# Revit family: IS_Extra_T3740_BIM_NL
name_source: partatom
category: Plumbing Fixtures
units: mm (PartAtom-declared; Revit-internal decimal feet)

## family parameters
Always vertical = No
Cut with Voids When Loaded = No
OmniClass Number = 23.45.05.14.14
OmniClass Title = Sinks/Lavatories
Part Type = Normal
Room Calculation Point = No
Round Connector Dimension = Use Diameter
Shared = No
Work Plane-Based = No

## types (1)
- T374001 - Extra Square Vessel 60x40 N with overflow and without tapholes - White
    Accessories = https://www.idealstandard.nl
    Afmetingen = 600 x 400 x 125 mm
    Afwerking = Weiß
    AreaMeasurement = Internal
    AreaUnits = Millimetres
    Artikelnummer = T374001
    Artikelomschrijving = Zusätzliches Gefäßbecken 60 x 40 cm, keine Hahnlöcher, kein Überlauf, glänzend weiß
    Artikelreferentie = Quadratisches Gefäß 60x40 N mit Überlauf und ohne Stichlöcher - Weiß
    AssetType = Fixed
    Auteur = Ideal Standard
    BIMObjectName = IS_IdealStandard_Wall-hungwashbasins_Extra_T3740
    BIMobject category = Basins
    BIMobject category code = sanitary-basins
    BIMobject main category = Sanitary
    BIMobject main category code = sanitary
    BarCode = 8014140467885
    Barcode = 8014140467885
    Beschrijvinggarantie = Herstellergarantie
    BimObjectNaam = IS_IdealStandard_Wall-hungwashbasins_Extra_T3740
    Brand = Ideal Standard
    Brand url = https://www.idealstandard.nl
    Breedte = 0
    BrutoGewicht = 0
    Color = White
    ConnectionType = Plumbing
    Cost = 0 $
    CurrencyUnit = €
    CurrentRevision = 1
    Date of publishing = 07/05/2021
    Description = Extra Square Vessel 60x40 N with overflow and without tapholes
    Diepte = 401 mm
    DurationUnit = Years
    DuurEenheid = Jahr
    Edition number = 1
    Eigenschappen = Zusätzliches Gefäßbecken 60 x 40 cm
    ExpectedLife = 99
    Features = Square Vessel 60x40 N with overflow and without tapholes - White
    Finish = White
    GTIN code = https://8014140467885
    Garantieonderdelen = 5
    Garantieunits = Jahr
    GemaaktOp = 07/05/2021
    Help = https://www.idealstandard.nl
    Hoogte = 125.001853140206
    Hulp = https://www.idealstandard.nl
    IFC Classification = Sanitary Terminal
    IfcExportAs = IfcSanitaryTerminalType
    IfcExportType = WASHHANDBASIN
    Installatieinstructies = https://www.idealstandard.nl
    Installation instructions = https://www.idealstandard.nl
    InstallationInstructions = https://www.idealstandard.nl
    Kleur = Weiß
    Lengte = 0 mm  [stored 0 ft]
    LinearUnits = millimetres
    MainColor = White
    MaintenanceInformation = https://www.idealstandard.nl
    Manufacturer = Ideal Standard
    Manufacturer name = Ideal Standard
    ManufacturerURL = https://www.idealstandard.nl
    Masterformat 2014 Code = 33 47 26.16
    Masterformat 2014 Description = Retention Basins
    Materiaal = FFC
    Material = Fine FireClay
    Material main = Fireclay
    MaterialThickness = 0 mm  [stored 0 ft]
    Merk = Ideal Standard
    Model = T374001
    ModelNumber = T3740
    ModelReference = Extra Square Basin
    Montageinstuctie = https://www.idealstandard.nl
    NBS Reference Code = 45-35-70/369
    NBS Reference Description = Wall hung wash basins
    Name = Wall-hungwashbasins_Extra_T3740_IdealStandard
    NettWeight = 12.70 Kg
    Nettogewicht = 12.7
    NominalDepth = 401 mm
    NominalHeight = 125 mm
    NominalWidth = 600 mm
    Normen = Wall-hungwashbasins_Extra_T3740_IdealStandard
    OmniClass Code = 23-39 29 13 21 19
    OmniClass Description = Surface Water Retention Basins
    OppervlakteEenheid = Millimeter
    Product Guid = b26f6d83-ca90-4835-933e-14a38d7c4193
    Product SKU = T3740
    Product certification = https://www.idealstandard.nl
    Product data url = https://bimobject.com
    Product family = Extra
    Product group = Washbasins
    Product name = Extra Vessel Basin 60 x 40cm, No Tap Holes, No Overflow, Glossy White
    Product url = https://www.idealstandard.nl
    ProductInformation = https://www.idealstandard.nl
    ProductSoort = Waschbecken
    Productinformatie = https://www.idealstandard.nl
    QR code = http://bimobject.com
    Referentie = T374001
    Revisie = 1
    Shape = Rectangular
    Size = 600 x 400 x 125 mm
    Space = Internal
    SpareParts = https://www.idealstandard.nl
    Technical description = https://www.idealstandard.nl
    Telefoonnummer = 077 355 08 08
    Typeconnectie = Sanitärinstallation
    UNSPSC Code = 301815
    URL = https://www.idealstandard.nl
    Uniclass 1.4 Code = L7212
    Uniclass 1.4 Description = Washbasins
    Uniclass 2.0 Code = PR-35-79-93
    Uniclass 2.0 Description = Wall-Hung Hand Rinse Basins
    Uniclass 2015 Code = Pr_40_20_96_95
    Uniclass 2015 Name = Wall-hung hand rinse basins
    Uniclass2015Beschrijving = Wall-hung hand rinse basins
    Uniclass2015Referentie = Pr_40_20_96_95
    Uniclass2015Version = v1.22
    Uniformat II Code = D2010
    Uniformat II Description = Plumbing Fixtures
    Urlproducent = https://www.idealstandard.nl
    ValutaEenheid = €
    Versie = 1
    Version = 1
    Vervangingskosten = 0
    VolumeUnits = Liters
    Volumeunits = Liter
    Vorm = Rechteckig
    WRASURL = https://www.wrasapprovals.co.uk
    WarrantyDescription = Manufacturer Warranty
    WarrantyDurationUnit = Years
    WashHandBasinMounting = WallHung
    WashHandBasinType = Washbasin
    Wisselstukken = https://www.idealstandard.nl
    Youtube clip = https://www.youtube.com

note: [stored X ft] marks values corroborated as IEEE doubles in the binary element streams (Revit-internal decimal feet)

## geometry (parser evidence)
native form markers: Sweep x3
no freeform markers — native parametric forms only
